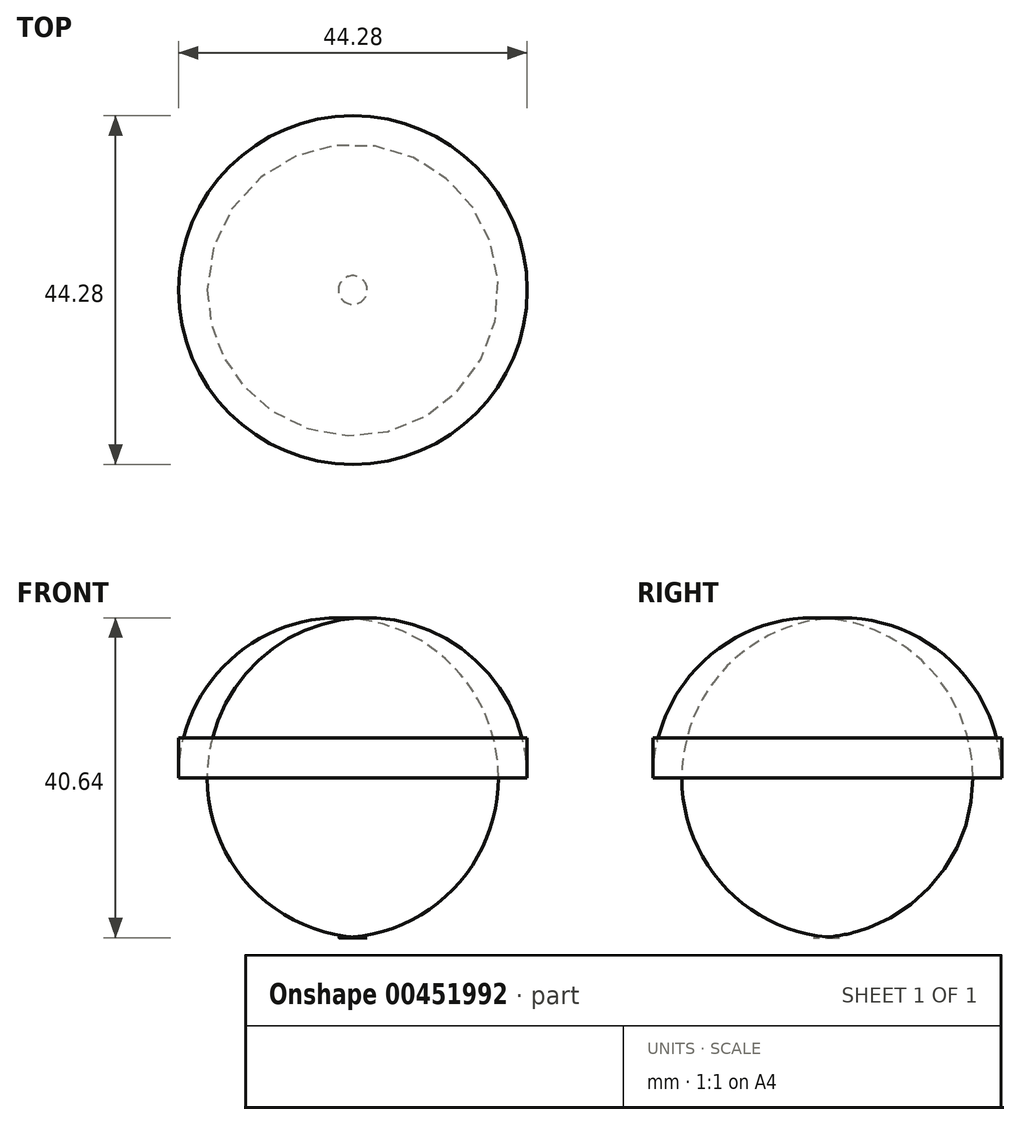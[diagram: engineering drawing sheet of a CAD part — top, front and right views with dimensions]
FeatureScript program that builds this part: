
annotation { "Feature Type Name" : "Feature", "Feature Type Description" : "" }
export const myFeature = defineFeature(function(context is Context, id is Id, definition is map)
    precondition{}
    {
        {
            var Q0;
            Q0=qCreatedBy(makeId("Top.planeOp"),FACE);
            var sketch = newSketch(context, id + "F0", { "sketchPlane" : qUnion([Q0])});
            skCircle(sketch, "E0", {"center": v(0, 0) * mm, "radius": 16.1 * mm});
            skSolve(sketch);
        }
        {
            var Q0;
            Q0=sQuery(id+"F0.wireOp",EDGE,"E0");
            extrude(context, id + "F1", {"bodyType" : ToolBodyType.SURFACE, "surfaceEntities" : qUnion([Q0]), "depth" : 177.8 * mm});
        }
        {
            var Q0;
            Q0=qCreatedBy(makeId("Top.planeOp"),FACE);
            var sketch = newSketch(context, id + "F2", { "sketchPlane" : qUnion([Q0])});
            skCircle(sketch, "E1", {"center": v(0, 0) * mm, "radius": 22.14 * mm});
            skSolve(sketch);
        }
        {
            var Q0;
            Q0=makeQuery(id+"F2.imprint","IMPRINT",FACE,{"disambiguationData":[TD([[makeQuery(id+"F2.imprint","IMPRINT",EDGE,{"derivedFrom":sQuery(id+"F2.wireOp",EDGE,"E1")}),1.0]])]});
            var Q1;
            Q1=sQuery(id+"F2.wireOp",EDGE,"E1");
            extrude(context, id + "F3", {"entities" : qUnion([Q0]), "surfaceEntities" : qUnion([Q1]), "oppositeDirection" : true, "depth" : 25.4 * mm});
        }
        {
            var Q0;
            Q0=makeQuery(id+"F3.opExtrude","CAP_EDGE",EDGE,{"disambiguationData":[OSD([sQuery(id+"F2.wireOp",EDGE,"E1")])],"isStart":false});
            fillet(context, id + "F4", {"entities" : qUnion([Q0]), "radius" : 20.32 * mm, "tangentPropagation" : true, "allowEdgeOverflow" : false});
        }
    });
